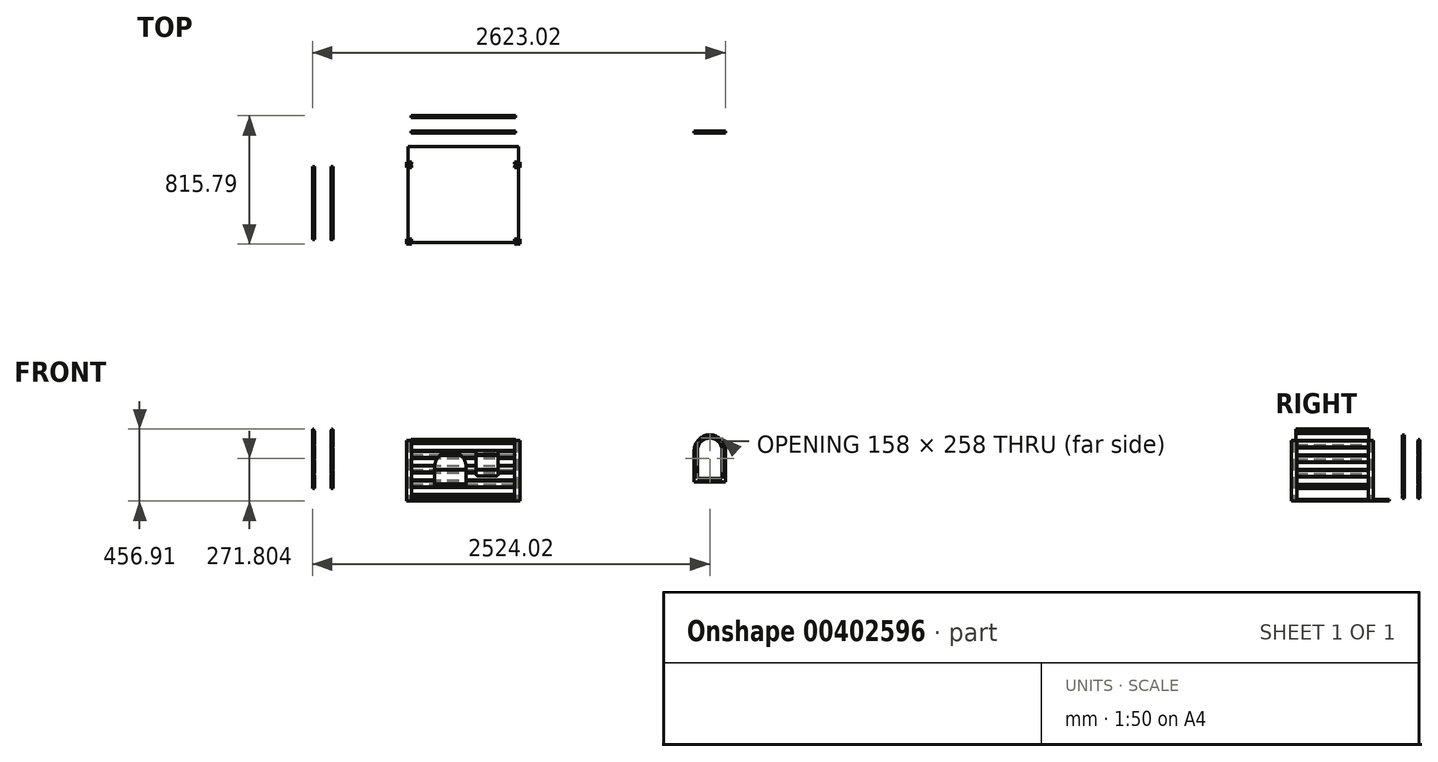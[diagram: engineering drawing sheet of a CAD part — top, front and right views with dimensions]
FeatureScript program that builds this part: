
annotation { "Feature Type Name" : "Feature", "Feature Type Description" : "" }
export const myFeature = defineFeature(function(context is Context, id is Id, definition is map)
    precondition{}
    {
        {
            var Q0;
            Q0=qCreatedBy(makeId("Top.planeOp"),FACE);
            var sketch = newSketch(context, id + "F0", { "sketchPlane" : qUnion([Q0])});
            skLineSegment(sketch, "E0.bottom", {"start": v(-350, -250) * mm, "end": v(350, -250) * mm});
            skLineSegment(sketch, "E0.top", {"start": v(-350, 360) * mm, "end": v(350, 360) * mm});
            skLineSegment(sketch, "E0.left", {"start": v(-350, -250) * mm, "end": v(-350, 360) * mm});
            skLineSegment(sketch, "E0.right", {"start": v(350, -250) * mm, "end": v(350, 360) * mm});
            skPoint(sketch, "E0.middle", {"position": v(0, 0) * mm});
            skSolve(sketch);
        }
        {
            var Q0;
            Q0=makeQuery(id+"F0.imprint","IMPRINT",FACE,{"disambiguationData":[TD([[makeQuery(id+"F0.imprint","IMPRINT",EDGE,{"derivedFrom":sQuery(id+"F0.wireOp",EDGE,"E0.bottom")}),1.0]])]});
            extrude(context, id + "F1", {"entities" : qUnion([Q0]), "depth" : 12 * mm});
        }
        {
            var Q0;
            Q0=makeQuery(id+"F1.opExtrude","CAP_FACE",FACE,{"disambiguationData":[OSD([sQuery(id+"F0.wireOp",EDGE,"E0.bottom"),sQuery(id+"F0.wireOp",EDGE,"E0.top"),sQuery(id+"F0.wireOp",EDGE,"E0.left"),sQuery(id+"F0.wireOp",EDGE,"E0.right")])],"isStart":true});
            var sketch = newSketch(context, id + "F2", { "sketchPlane" : qUnion([Q0])});
            skLineSegment(sketch, "E1.bottom", {"start": v(-326.75, 226.75) * mm, "end": v(-337.5, 226.75) * mm});
            skLineSegment(sketch, "E1.top", {"start": v(-326.75, 260.75) * mm, "end": v(-360.75, 260.75) * mm});
            skLineSegment(sketch, "E1.left", {"start": v(-326.75, 226.75) * mm, "end": v(-326.75, 237.5) * mm});
            skLineSegment(sketch, "E1.right", {"start": v(-360.75, 226.75) * mm, "end": v(-360.75, 260.75) * mm});
            skPoint(sketch, "E1.middle", {"position": v(-343.75, 243.75) * mm});
            skLineSegment(sketch, "E2.bottom", {"start": v(-337.5, 231.75) * mm, "end": v(-350, 231.75) * mm});
            skLineSegment(sketch, "E2.left", {"start": v(-337.5, 231.75) * mm, "end": v(-337.5, 226.75) * mm});
            skLineSegment(sketch, "E2.right", {"start": v(-350, 231.75) * mm, "end": v(-350, 226.75) * mm});
            skPoint(sketch, "E2.middle", {"position": v(-343.75, 226.75) * mm});
            skLineSegment(sketch, "E3.bottom", {"start": v(-331.75, 250) * mm, "end": v(-326.75, 250) * mm});
            skLineSegment(sketch, "E3.top", {"start": v(-331.75, 237.5) * mm, "end": v(-326.75, 237.5) * mm});
            skLineSegment(sketch, "E3.left", {"start": v(-331.75, 250) * mm, "end": v(-331.75, 237.5) * mm});
            skPoint(sketch, "E3.middle", {"position": v(-326.75, 243.75) * mm});
            skLineSegment(sketch, "E4", {"start": v(-350, 250) * mm, "end": v(-350, 231.75) * mm});
            skLineSegment(sketch, "E5.trimOffspring", {"start": v(-350, 226.75) * mm, "end": v(-360.75, 226.75) * mm});
            skLineSegment(sketch, "E6.trimOffspring", {"start": v(-326.75, 250) * mm, "end": v(-326.75, 260.75) * mm});
            skPoint(sketch, "E7", {"position": v(-350, 231.75) * mm});
            skLineSegment(sketch, "E8.MirrorCS", {"start": v(350, 231.75) * mm, "end": v(350, 226.75) * mm});
            skLineSegment(sketch, "E9.MirrorCS", {"start": v(337.5, 231.75) * mm, "end": v(350, 231.75) * mm});
            skLineSegment(sketch, "E10.MirrorCS", {"start": v(331.75, 250) * mm, "end": v(331.75, 237.5) * mm});
            skLineSegment(sketch, "E11.MirrorCS", {"start": v(331.75, 250) * mm, "end": v(326.75, 250) * mm});
            skLineSegment(sketch, "E12.MirrorCS", {"start": v(331.75, 237.5) * mm, "end": v(326.75, 237.5) * mm});
            skLineSegment(sketch, "E13.MirrorCS", {"start": v(337.5, 231.75) * mm, "end": v(337.5, 226.75) * mm});
            skLineSegment(sketch, "E14.MirrorCS", {"start": v(326.75, 226.75) * mm, "end": v(326.75, 237.5) * mm});
            skLineSegment(sketch, "E15.MirrorCS", {"start": v(326.75, 250) * mm, "end": v(326.75, 260.75) * mm});
            skLineSegment(sketch, "E16.MirrorCS", {"start": v(326.75, 226.75) * mm, "end": v(337.5, 226.75) * mm});
            skLineSegment(sketch, "E17.MirrorCS", {"start": v(350, 226.75) * mm, "end": v(360.75, 226.75) * mm});
            skLineSegment(sketch, "E18.MirrorCS", {"start": v(350, 250) * mm, "end": v(350, 231.75) * mm});
            skPoint(sketch, "E19.MirrorP", {"position": v(350, 231.75) * mm});
            skLineSegment(sketch, "E20.MirrorCS", {"start": v(326.75, 260.75) * mm, "end": v(360.75, 260.75) * mm});
            skLineSegment(sketch, "E21.MirrorCS", {"start": v(360.75, 226.75) * mm, "end": v(360.75, 260.75) * mm});
            skPoint(sketch, "E22.MirrorP", {"position": v(343.75, 243.75) * mm});
            skPoint(sketch, "E23.MirrorP", {"position": v(343.75, 226.75) * mm});
            skPoint(sketch, "E24.MirrorP", {"position": v(326.75, 243.75) * mm});
            skLineSegment(sketch, "E25.MirrorCS", {"start": v(331.75, -250) * mm, "end": v(331.75, -237.5) * mm});
            skLineSegment(sketch, "E26.MirrorCS", {"start": v(331.75, -250) * mm, "end": v(326.75, -250) * mm});
            skLineSegment(sketch, "E27.MirrorCS", {"start": v(326.75, -250) * mm, "end": v(326.75, -260.75) * mm});
            skLineSegment(sketch, "E28.MirrorCS", {"start": v(350, -250) * mm, "end": v(350, -231.75) * mm});
            skLineSegment(sketch, "E29.MirrorCS", {"start": v(326.75, -260.75) * mm, "end": v(360.75, -260.75) * mm});
            skLineSegment(sketch, "E30.MirrorCS", {"start": v(360.75, -226.75) * mm, "end": v(360.75, -260.75) * mm});
            skLineSegment(sketch, "E31.MirrorCS", {"start": v(350, -231.75) * mm, "end": v(350, -226.75) * mm});
            skLineSegment(sketch, "E32.MirrorCS", {"start": v(-350, -231.75) * mm, "end": v(-350, -226.75) * mm});
            skLineSegment(sketch, "E33.MirrorCS", {"start": v(337.5, -231.75) * mm, "end": v(350, -231.75) * mm});
            skLineSegment(sketch, "E34.MirrorCS", {"start": v(331.75, -237.5) * mm, "end": v(326.75, -237.5) * mm});
            skLineSegment(sketch, "E35.MirrorCS", {"start": v(-337.5, -231.75) * mm, "end": v(-350, -231.75) * mm});
            skLineSegment(sketch, "E36.MirrorCS", {"start": v(-331.75, -250) * mm, "end": v(-331.75, -237.5) * mm});
            skLineSegment(sketch, "E37.MirrorCS", {"start": v(337.5, -231.75) * mm, "end": v(337.5, -226.75) * mm});
            skLineSegment(sketch, "E38.MirrorCS", {"start": v(-331.75, -237.5) * mm, "end": v(-326.75, -237.5) * mm});
            skLineSegment(sketch, "E39.MirrorCS", {"start": v(-337.5, -231.75) * mm, "end": v(-337.5, -226.75) * mm});
            skLineSegment(sketch, "E40.MirrorCS", {"start": v(-331.75, -250) * mm, "end": v(-326.75, -250) * mm});
            skLineSegment(sketch, "E41.MirrorCS", {"start": v(326.75, -226.75) * mm, "end": v(337.5, -226.75) * mm});
            skLineSegment(sketch, "E42.MirrorCS", {"start": v(326.75, -226.75) * mm, "end": v(326.75, -237.5) * mm});
            skLineSegment(sketch, "E43.MirrorCS", {"start": v(-326.75, -226.75) * mm, "end": v(-337.5, -226.75) * mm});
            skLineSegment(sketch, "E44.MirrorCS", {"start": v(-326.75, -226.75) * mm, "end": v(-326.75, -237.5) * mm});
            skLineSegment(sketch, "E45.MirrorCS", {"start": v(-326.75, -250) * mm, "end": v(-326.75, -260.75) * mm});
            skLineSegment(sketch, "E46.MirrorCS", {"start": v(350, -226.75) * mm, "end": v(360.75, -226.75) * mm});
            skLineSegment(sketch, "E47.MirrorCS", {"start": v(-350, -226.75) * mm, "end": v(-360.75, -226.75) * mm});
            skLineSegment(sketch, "E48.MirrorCS", {"start": v(-350, -250) * mm, "end": v(-350, -231.75) * mm});
            skPoint(sketch, "E49.MirrorP", {"position": v(343.75, -226.75) * mm});
            skPoint(sketch, "E50.MirrorP", {"position": v(-326.75, -243.75) * mm});
            skLineSegment(sketch, "E51.MirrorCS", {"start": v(-360.75, -226.75) * mm, "end": v(-360.75, -260.75) * mm});
            skLineSegment(sketch, "E52.MirrorCS", {"start": v(-326.75, -260.75) * mm, "end": v(-360.75, -260.75) * mm});
            skPoint(sketch, "E53.MirrorP", {"position": v(350, -231.75) * mm});
            skPoint(sketch, "E54.MirrorP", {"position": v(-343.75, -226.75) * mm});
            skPoint(sketch, "E55.MirrorP", {"position": v(-343.75, -243.75) * mm});
            skPoint(sketch, "E56.MirrorP", {"position": v(326.75, -243.75) * mm});
            skPoint(sketch, "E57.MirrorP", {"position": v(-350, -231.75) * mm});
            skPoint(sketch, "E58.MirrorP", {"position": v(343.75, -243.75) * mm});
            skLineSegment(sketch, "E59", {"start": v(-350, -250) * mm, "end": v(-350, -260.75) * mm});
            skLineSegment(sketch, "E60", {"start": v(350, -250) * mm, "end": v(350, -260.75) * mm});
            skSolve(sketch);
        }
        {
            var Q0;
            Q0=makeQuery(id+"F2.imprint","IMPRINT",FACE,{"disambiguationData":[TD([[makeQuery(id+"F2.imprint","IMPRINT",EDGE,{"derivedFrom":sQuery(id+"F2.wireOp",EDGE,"E1.top")}),1.0]])]});
            var Q1;
            Q1=makeQuery(id+"F2.imprint","IMPRINT",FACE,{"disambiguationData":[TD([[makeQuery(id+"F2.imprint","IMPRINT",EDGE,{"derivedFrom":sQuery(id+"F2.wireOp",EDGE,"E32.MirrorCS")}),-1.0]])]});
            var Q2;
            Q2=makeQuery(id+"F2.imprint","IMPRINT",FACE,{"disambiguationData":[TD([[makeQuery(id+"F2.imprint","IMPRINT",EDGE,{"derivedFrom":sQuery(id+"F2.wireOp",EDGE,"E8.MirrorCS")}),1.0]])]});
            var Q3;
            Q3=makeQuery(id+"F2.imprint","IMPRINT",FACE,{"disambiguationData":[TD([[makeQuery(id+"F2.imprint","IMPRINT",EDGE,{"derivedFrom":sQuery(id+"F2.wireOp",EDGE,"E28.MirrorCS")}),1.0]])]});
            extrude(context, id + "F3", {"entities" : qUnion([Q0, Q1, Q2, Q3]), "oppositeDirection" : true, "depth" : 384 * mm});
        }
        {
            var Q0;
            Q0=makeQuery(id+"F2.imprint","IMPRINT",FACE,{"disambiguationData":[TD([[makeQuery(id+"F2.imprint","IMPRINT",EDGE,{"derivedFrom":sQuery(id+"F2.wireOp",EDGE,"E9.MirrorCS")}),1.0]])]});
            var Q1;
            Q1=makeQuery(id+"F2.imprint","IMPRINT",FACE,{"disambiguationData":[TD([[makeQuery(id+"F2.imprint","IMPRINT",EDGE,{"derivedFrom":sQuery(id+"F2.wireOp",EDGE,"E1.bottom")}),-1.0]])]});
            var Q2;
            {var subQ1=sQuery(id+"F2.wireOp",EDGE,"E25.MirrorCS");Q2=makeQuery(id+"F2.imprint","IMPRINT",FACE,{"disambiguationData":[TD([[makeQuery(id+"F2.imprint","IMPRINT",EDGE,{"derivedFrom":subQ1}),-1.0]])]});}
            var Q3;
            Q3=makeQuery(id+"F2.imprint","IMPRINT",FACE,{"disambiguationData":[TD([[makeQuery(id+"F2.imprint","IMPRINT",EDGE,{"derivedFrom":sQuery(id+"F2.wireOp",EDGE,"E35.MirrorCS")}),1.0]])]});
            var Q4;
            {var subQ3=sQuery(id+"F2.wireOp",EDGE,"E40.MirrorCS");Q4=makeQuery(id+"F2.imprint","IMPRINT",FACE,{"disambiguationData":[TD([[makeQuery(id+"F2.imprint","IMPRINT",EDGE,{"derivedFrom":subQ3}),-1.0]])]});}
            extrude(context, id + "F4", {"entities" : qUnion([Q0, Q1, Q2, Q3, Q4]), "oppositeDirection" : true, "depth" : 384 * mm, "hasSecondDirection" : true, "secondDirectionOppositeDirection" : true, "secondDirectionDepth" : 12 * mm});
        }
        {
            var Q0;
            Q0=makeQuery(id+"F4.opExtrude","SWEPT_FACE",FACE,{"disambiguationData":[OSD([sQuery(id+"F2.wireOp",EDGE,"E33.MirrorCS")])]});
            var sketch = newSketch(context, id + "F5", { "sketchPlane" : qUnion([Q0])});
            skLineSegment(sketch, "E61", {"start": v(-893, 200.64) * mm, "end": v(-893, 47.68) * mm});
            skLineSegment(sketch, "E62.MirrorCS", {"start": v(-951.9, 177.9) * mm, "end": v(-953.9, 177.9) * mm});
            skLineSegment(sketch, "E63.MirrorCS", {"start": v(-951.9, 177.9) * mm, "end": v(-949.9, 177.9) * mm});
            skLineSegment(sketch, "E64.MirrorCS", {"start": v(-949.9, 177.9) * mm, "end": v(-953.9, 177.9) * mm});
            skLineSegment(sketch, "E65.MirrorCS", {"start": v(-949.9, 170.9) * mm, "end": v(-949.64, 170.9) * mm});
            skLineSegment(sketch, "E66.MirrorCS", {"start": v(-953.9, 177.9) * mm, "end": v(-953.9, 174.9) * mm});
            skLineSegment(sketch, "E67.MirrorCS", {"start": v(-949.9, 81.9) * mm, "end": v(-949.9, 84.9) * mm});
            skLineSegment(sketch, "E68.MirrorCS", {"start": v(-953.9, 81.9) * mm, "end": v(-953.9, 84.9) * mm});
            skLineSegment(sketch, "E69.MirrorCS", {"start": v(-953.9, 84.9) * mm, "end": v(-949.9, 84.9) * mm});
            skLineSegment(sketch, "E70.MirrorCS", {"start": v(-945.64, 81.9) * mm, "end": v(-949.9, 81.9) * mm});
            skLineSegment(sketch, "E71.MirrorCS", {"start": v(-953.9, 81.9) * mm, "end": v(-958.14, 81.9) * mm});
            skArc(sketch, "E72.MirrorCS", {"start": v(-958.14, 152.4) * mm, "mid": v(-955.64, 154.9) * mm, "end": v(-958.14, 157.4) * mm});
            skArc(sketch, "E73.MirrorCS", {"start": v(-945.64, 166.9) * mm, "mid": v(-946.82, 169.73) * mm, "end": v(-949.64, 170.9) * mm});
            skArc(sketch, "E74.MirrorCS", {"start": v(-958.14, 102.4) * mm, "mid": v(-955.64, 104.9) * mm, "end": v(-958.14, 107.4) * mm});
            skLineSegment(sketch, "E75.MirrorCS", {"start": v(-958.14, 129.9) * mm, "end": v(-958.14, 107.4) * mm});
            skLineSegment(sketch, "E76.MirrorCS", {"start": v(-945.64, 81.9) * mm, "end": v(-945.64, 166.9) * mm});
            skLineSegment(sketch, "E77.MirrorCS", {"start": v(-949.9, 177.9) * mm, "end": v(-949.9, 170.9) * mm});
            skPoint(sketch, "E78.MirrorP", {"position": v(-953.9, 80.4) * mm});
            skPoint(sketch, "E79.MirrorP", {"position": v(-945.64, 170.9) * mm});
            skPoint(sketch, "E80.MirrorP", {"position": v(-949.9, 80.4) * mm});
            skLineSegment(sketch, "E81.MirrorCS", {"start": v(-958.14, 81.9) * mm, "end": v(-958.14, 102.4) * mm});
            skLineSegment(sketch, "E82.MirrorCS", {"start": v(-958.14, 107.4) * mm, "end": v(-958.14, 154.9) * mm});
            skPoint(sketch, "E83.MirrorP", {"position": v(-951.9, 81.9) * mm});
            skLineSegment(sketch, "E84.MirrorCS", {"start": v(-958.14, 129.9) * mm, "end": v(-958.14, 152.4) * mm});
            skLineSegment(sketch, "E85.MirrorCS", {"start": v(-958.14, 157.4) * mm, "end": v(-958.14, 174.9) * mm});
            skPoint(sketch, "E86.MirrorP", {"position": v(-951.9, 129.9) * mm});
            skPoint(sketch, "E87.MirrorP", {"position": v(-958.14, 177.9) * mm});
            skLineSegment(sketch, "E88.MirrorCS", {"start": v(-951.9, 270.9) * mm, "end": v(-953.9, 270.9) * mm});
            skLineSegment(sketch, "E89.MirrorCS", {"start": v(-951.9, 270.9) * mm, "end": v(-949.9, 270.9) * mm});
            skLineSegment(sketch, "E90.MirrorCS", {"start": v(-949.9, 270.9) * mm, "end": v(-953.9, 270.9) * mm});
            skLineSegment(sketch, "E91.MirrorCS", {"start": v(-949.9, 263.9) * mm, "end": v(-949.64, 263.9) * mm});
            skLineSegment(sketch, "E92.MirrorCS", {"start": v(-953.9, 270.9) * mm, "end": v(-953.9, 267.9) * mm});
            skLineSegment(sketch, "E93.MirrorCS", {"start": v(-949.9, 174.9) * mm, "end": v(-949.9, 177.9) * mm});
            skLineSegment(sketch, "E94.MirrorCS", {"start": v(-953.9, 174.9) * mm, "end": v(-953.9, 177.9) * mm});
            skLineSegment(sketch, "E95.MirrorCS", {"start": v(-953.9, 177.9) * mm, "end": v(-949.9, 177.9) * mm});
            skLineSegment(sketch, "E96.MirrorCS", {"start": v(-945.64, 174.9) * mm, "end": v(-949.9, 174.9) * mm});
            skArc(sketch, "E97.MirrorCS", {"start": v(-958.14, 245.4) * mm, "mid": v(-955.64, 247.9) * mm, "end": v(-958.14, 250.4) * mm});
            skArc(sketch, "E98.MirrorCS", {"start": v(-945.64, 259.9) * mm, "mid": v(-946.82, 262.73) * mm, "end": v(-949.64, 263.9) * mm});
            skArc(sketch, "E99.MirrorCS", {"start": v(-958.14, 195.4) * mm, "mid": v(-955.64, 197.9) * mm, "end": v(-958.14, 200.4) * mm});
            skLineSegment(sketch, "E100.MirrorCS", {"start": v(-958.14, 222.9) * mm, "end": v(-958.14, 200.4) * mm});
            skLineSegment(sketch, "E101.MirrorCS", {"start": v(-945.64, 174.9) * mm, "end": v(-945.64, 259.9) * mm});
            skLineSegment(sketch, "E102.MirrorCS", {"start": v(-949.9, 270.9) * mm, "end": v(-949.9, 263.9) * mm});
            skPoint(sketch, "E103.MirrorP", {"position": v(-953.9, 173.4) * mm});
            skPoint(sketch, "E104.MirrorP", {"position": v(-945.64, 263.9) * mm});
            skPoint(sketch, "E105.MirrorP", {"position": v(-949.9, 173.4) * mm});
            skLineSegment(sketch, "E106.MirrorCS", {"start": v(-958.14, 174.9) * mm, "end": v(-958.14, 195.4) * mm});
            skLineSegment(sketch, "E107.MirrorCS", {"start": v(-958.14, 200.4) * mm, "end": v(-958.14, 247.9) * mm});
            skPoint(sketch, "E108.MirrorP", {"position": v(-951.9, 174.9) * mm});
            skLineSegment(sketch, "E109.MirrorCS", {"start": v(-958.14, 222.9) * mm, "end": v(-958.14, 245.4) * mm});
            skLineSegment(sketch, "E110.MirrorCS", {"start": v(-958.14, 250.4) * mm, "end": v(-958.14, 267.9) * mm});
            skPoint(sketch, "E111.MirrorP", {"position": v(-951.9, 222.9) * mm});
            skPoint(sketch, "E112.MirrorP", {"position": v(-958.14, 270.9) * mm});
            skLineSegment(sketch, "E113.MirrorCS", {"start": v(-951.9, 363.9) * mm, "end": v(-953.9, 363.9) * mm});
            skLineSegment(sketch, "E114.MirrorCS", {"start": v(-951.9, 363.9) * mm, "end": v(-949.9, 363.9) * mm});
            skLineSegment(sketch, "E115.MirrorCS", {"start": v(-949.9, 363.9) * mm, "end": v(-953.9, 363.9) * mm});
            skLineSegment(sketch, "E116.MirrorCS", {"start": v(-949.9, 356.9) * mm, "end": v(-949.64, 356.9) * mm});
            skLineSegment(sketch, "E117.MirrorCS", {"start": v(-953.9, 363.9) * mm, "end": v(-953.9, 360.9) * mm});
            skLineSegment(sketch, "E118.MirrorCS", {"start": v(-949.9, 267.9) * mm, "end": v(-949.9, 270.9) * mm});
            skLineSegment(sketch, "E119.MirrorCS", {"start": v(-953.9, 267.9) * mm, "end": v(-953.9, 270.9) * mm});
            skLineSegment(sketch, "E120.MirrorCS", {"start": v(-953.9, 270.9) * mm, "end": v(-949.9, 270.9) * mm});
            skLineSegment(sketch, "E121.MirrorCS", {"start": v(-945.64, 267.9) * mm, "end": v(-949.9, 267.9) * mm});
            skArc(sketch, "E122.MirrorCS", {"start": v(-958.14, 338.4) * mm, "mid": v(-955.64, 340.9) * mm, "end": v(-958.14, 343.4) * mm});
            skArc(sketch, "E123.MirrorCS", {"start": v(-945.64, 352.9) * mm, "mid": v(-946.82, 355.73) * mm, "end": v(-949.64, 356.9) * mm});
            skArc(sketch, "E124.MirrorCS", {"start": v(-958.14, 288.4) * mm, "mid": v(-955.64, 290.9) * mm, "end": v(-958.14, 293.4) * mm});
            skLineSegment(sketch, "E125.MirrorCS", {"start": v(-958.14, 315.9) * mm, "end": v(-958.14, 293.4) * mm});
            skLineSegment(sketch, "E126.MirrorCS", {"start": v(-945.64, 267.9) * mm, "end": v(-945.64, 352.9) * mm});
            skLineSegment(sketch, "E127.MirrorCS", {"start": v(-949.9, 363.9) * mm, "end": v(-949.9, 356.9) * mm});
            skPoint(sketch, "E128.MirrorP", {"position": v(-953.9, 266.4) * mm});
            skPoint(sketch, "E129.MirrorP", {"position": v(-945.64, 356.9) * mm});
            skPoint(sketch, "E130.MirrorP", {"position": v(-949.9, 266.4) * mm});
            skLineSegment(sketch, "E131.MirrorCS", {"start": v(-958.14, 267.9) * mm, "end": v(-958.14, 288.4) * mm});
            skLineSegment(sketch, "E132.MirrorCS", {"start": v(-958.14, 293.4) * mm, "end": v(-958.14, 340.9) * mm});
            skPoint(sketch, "E133.MirrorP", {"position": v(-951.9, 267.9) * mm});
            skLineSegment(sketch, "E134.MirrorCS", {"start": v(-958.14, 315.9) * mm, "end": v(-958.14, 338.4) * mm});
            skLineSegment(sketch, "E135.MirrorCS", {"start": v(-958.14, 343.4) * mm, "end": v(-958.14, 360.9) * mm});
            skPoint(sketch, "E136.MirrorP", {"position": v(-951.9, 315.9) * mm});
            skPoint(sketch, "E137.MirrorP", {"position": v(-958.14, 363.9) * mm});
            skLineSegment(sketch, "E138.MirrorCS", {"start": v(-951.9, 456.9) * mm, "end": v(-953.9, 456.9) * mm});
            skLineSegment(sketch, "E139.MirrorCS", {"start": v(-951.9, 456.9) * mm, "end": v(-949.9, 456.9) * mm});
            skLineSegment(sketch, "E140.MirrorCS", {"start": v(-949.9, 456.9) * mm, "end": v(-953.9, 456.9) * mm});
            skLineSegment(sketch, "E141.MirrorCS", {"start": v(-949.9, 449.9) * mm, "end": v(-949.64, 449.9) * mm});
            skLineSegment(sketch, "E142.MirrorCS", {"start": v(-953.9, 456.9) * mm, "end": v(-953.9, 453.9) * mm});
            skLineSegment(sketch, "E143.MirrorCS", {"start": v(-949.9, 360.9) * mm, "end": v(-949.9, 363.9) * mm});
            skLineSegment(sketch, "E144.MirrorCS", {"start": v(-953.9, 360.9) * mm, "end": v(-953.9, 363.9) * mm});
            skLineSegment(sketch, "E145.MirrorCS", {"start": v(-953.9, 363.9) * mm, "end": v(-949.9, 363.9) * mm});
            skLineSegment(sketch, "E146.MirrorCS", {"start": v(-945.64, 360.9) * mm, "end": v(-949.9, 360.9) * mm});
            skArc(sketch, "E147.MirrorCS", {"start": v(-958.14, 431.4) * mm, "mid": v(-955.64, 433.9) * mm, "end": v(-958.14, 436.4) * mm});
            skArc(sketch, "E148.MirrorCS", {"start": v(-945.64, 445.9) * mm, "mid": v(-946.82, 448.73) * mm, "end": v(-949.64, 449.9) * mm});
            skArc(sketch, "E149.MirrorCS", {"start": v(-958.14, 381.4) * mm, "mid": v(-955.64, 383.9) * mm, "end": v(-958.14, 386.4) * mm});
            skLineSegment(sketch, "E150.MirrorCS", {"start": v(-958.14, 408.9) * mm, "end": v(-958.14, 386.4) * mm});
            skLineSegment(sketch, "E151.MirrorCS", {"start": v(-945.64, 360.9) * mm, "end": v(-945.64, 445.9) * mm});
            skLineSegment(sketch, "E152.MirrorCS", {"start": v(-949.9, 456.9) * mm, "end": v(-949.9, 449.9) * mm});
            skPoint(sketch, "E153.MirrorP", {"position": v(-953.9, 359.4) * mm});
            skPoint(sketch, "E154.MirrorP", {"position": v(-945.64, 449.9) * mm});
            skPoint(sketch, "E155.MirrorP", {"position": v(-949.9, 359.4) * mm});
            skLineSegment(sketch, "E156.MirrorCS", {"start": v(-958.14, 360.9) * mm, "end": v(-958.14, 381.4) * mm});
            skLineSegment(sketch, "E157.MirrorCS", {"start": v(-958.14, 386.4) * mm, "end": v(-958.14, 433.9) * mm});
            skPoint(sketch, "E158.MirrorP", {"position": v(-951.9, 360.9) * mm});
            skLineSegment(sketch, "E159.MirrorCS", {"start": v(-958.14, 408.9) * mm, "end": v(-958.14, 431.4) * mm});
            skLineSegment(sketch, "E160.MirrorCS", {"start": v(-958.14, 436.4) * mm, "end": v(-958.14, 453.9) * mm});
            skPoint(sketch, "E161.MirrorP", {"position": v(-951.9, 408.9) * mm});
            skPoint(sketch, "E162.MirrorP", {"position": v(-958.14, 456.9) * mm});
            skLineSegment(sketch, "E163", {"start": v(-953.9, 453.9) * mm, "end": v(-958.14, 453.9) * mm});
            skLineSegment(sketch, "E164.MirrorCS", {"start": v(-836.12, 270.9) * mm, "end": v(-832.12, 270.9) * mm});
            skLineSegment(sketch, "E165.MirrorCS", {"start": v(-834.12, 363.9) * mm, "end": v(-832.12, 363.9) * mm});
            skLineSegment(sketch, "E166.MirrorCS", {"start": v(-832.12, 270.9) * mm, "end": v(-832.12, 267.9) * mm});
            skLineSegment(sketch, "E167.MirrorCS", {"start": v(-832.12, 363.9) * mm, "end": v(-836.12, 363.9) * mm});
            skLineSegment(sketch, "E168.MirrorCS", {"start": v(-836.12, 263.9) * mm, "end": v(-836.37, 263.9) * mm});
            skLineSegment(sketch, "E169.MirrorCS", {"start": v(-834.12, 270.9) * mm, "end": v(-836.12, 270.9) * mm});
            skLineSegment(sketch, "E170.MirrorCS", {"start": v(-834.12, 363.9) * mm, "end": v(-836.12, 363.9) * mm});
            skLineSegment(sketch, "E171.MirrorCS", {"start": v(-832.12, 270.9) * mm, "end": v(-836.12, 270.9) * mm});
            skLineSegment(sketch, "E172.MirrorCS", {"start": v(-836.12, 363.9) * mm, "end": v(-832.12, 363.9) * mm});
            skLineSegment(sketch, "E173.MirrorCS", {"start": v(-834.12, 270.9) * mm, "end": v(-832.12, 270.9) * mm});
            skLineSegment(sketch, "E174.MirrorCS", {"start": v(-836.12, 267.9) * mm, "end": v(-836.12, 270.9) * mm});
            skLineSegment(sketch, "E175.MirrorCS", {"start": v(-836.12, 360.9) * mm, "end": v(-836.12, 363.9) * mm});
            skLineSegment(sketch, "E176.MirrorCS", {"start": v(-832.12, 267.9) * mm, "end": v(-832.12, 270.9) * mm});
            skLineSegment(sketch, "E177.MirrorCS", {"start": v(-832.12, 363.9) * mm, "end": v(-832.12, 360.9) * mm});
            skLineSegment(sketch, "E178.MirrorCS", {"start": v(-836.12, 270.9) * mm, "end": v(-836.12, 263.9) * mm});
            skLineSegment(sketch, "E179.MirrorCS", {"start": v(-836.12, 363.9) * mm, "end": v(-836.12, 356.9) * mm});
            skLineSegment(sketch, "E180.MirrorCS", {"start": v(-832.12, 177.9) * mm, "end": v(-836.12, 177.9) * mm});
            skLineSegment(sketch, "E181.MirrorCS", {"start": v(-840.37, 267.9) * mm, "end": v(-836.12, 267.9) * mm});
            skLineSegment(sketch, "E182.MirrorCS", {"start": v(-836.12, 356.9) * mm, "end": v(-836.37, 356.9) * mm});
            skArc(sketch, "E183.MirrorCS", {"start": v(-840.37, 259.9) * mm, "mid": v(-839.2, 262.73) * mm, "end": v(-836.37, 263.9) * mm});
            skLineSegment(sketch, "E184.MirrorCS", {"start": v(-836.12, 174.9) * mm, "end": v(-836.12, 177.9) * mm});
            skArc(sketch, "E185.MirrorCS", {"start": v(-840.37, 352.9) * mm, "mid": v(-839.2, 355.73) * mm, "end": v(-836.37, 356.9) * mm});
            skLineSegment(sketch, "E186.MirrorCS", {"start": v(-840.37, 360.9) * mm, "end": v(-836.12, 360.9) * mm});
            skLineSegment(sketch, "E187.MirrorCS", {"start": v(-832.12, 360.9) * mm, "end": v(-832.12, 363.9) * mm});
            skLineSegment(sketch, "E188.MirrorCS", {"start": v(-834.12, 177.9) * mm, "end": v(-832.12, 177.9) * mm});
            skLineSegment(sketch, "E189.MirrorCS", {"start": v(-836.12, 177.9) * mm, "end": v(-836.12, 170.9) * mm});
            skLineSegment(sketch, "E190.MirrorCS", {"start": v(-832.12, 174.9) * mm, "end": v(-832.12, 177.9) * mm});
            skLineSegment(sketch, "E191.MirrorCS", {"start": v(-836.12, 177.9) * mm, "end": v(-832.12, 177.9) * mm});
            skLineSegment(sketch, "E192.MirrorCS", {"start": v(-834.12, 177.9) * mm, "end": v(-836.12, 177.9) * mm});
            skLineSegment(sketch, "E193.MirrorCS", {"start": v(-836.12, 170.9) * mm, "end": v(-836.37, 170.9) * mm});
            skLineSegment(sketch, "E194.MirrorCS", {"start": v(-840.37, 174.9) * mm, "end": v(-836.12, 174.9) * mm});
            skArc(sketch, "E195.MirrorCS", {"start": v(-840.37, 166.9) * mm, "mid": v(-839.2, 169.73) * mm, "end": v(-836.37, 170.9) * mm});
            skLineSegment(sketch, "E196.MirrorCS", {"start": v(-832.12, 177.9) * mm, "end": v(-832.12, 174.9) * mm});
            skLineSegment(sketch, "E197.MirrorCS", {"start": v(-834.12, 456.9) * mm, "end": v(-832.12, 456.9) * mm});
            skLineSegment(sketch, "E198.MirrorCS", {"start": v(-832.12, 84.9) * mm, "end": v(-836.12, 84.9) * mm});
            skLineSegment(sketch, "E199.MirrorCS", {"start": v(-834.12, 456.9) * mm, "end": v(-836.12, 456.9) * mm});
            skLineSegment(sketch, "E200.MirrorCS", {"start": v(-832.12, 456.9) * mm, "end": v(-832.12, 453.9) * mm});
            skLineSegment(sketch, "E201.MirrorCS", {"start": v(-827.87, 157.4) * mm, "end": v(-827.87, 174.9) * mm});
            skLineSegment(sketch, "E202.MirrorCS", {"start": v(-836.12, 81.9) * mm, "end": v(-836.12, 84.9) * mm});
            skLineSegment(sketch, "E203.MirrorCS", {"start": v(-836.12, 456.9) * mm, "end": v(-832.12, 456.9) * mm});
            skArc(sketch, "E204.MirrorCS", {"start": v(-840.37, 445.9) * mm, "mid": v(-839.2, 448.73) * mm, "end": v(-836.37, 449.9) * mm});
            skLineSegment(sketch, "E205.MirrorCS", {"start": v(-827.87, 250.4) * mm, "end": v(-827.87, 267.9) * mm});
            skLineSegment(sketch, "E206.MirrorCS", {"start": v(-827.87, 436.4) * mm, "end": v(-827.87, 453.9) * mm});
            skLineSegment(sketch, "E207.MirrorCS", {"start": v(-836.12, 456.9) * mm, "end": v(-836.12, 449.9) * mm});
            skLineSegment(sketch, "E208.MirrorCS", {"start": v(-836.12, 449.9) * mm, "end": v(-836.37, 449.9) * mm});
            skLineSegment(sketch, "E209.MirrorCS", {"start": v(-832.12, 81.9) * mm, "end": v(-832.12, 84.9) * mm});
            skArc(sketch, "E210.MirrorCS", {"start": v(-827.87, 152.4) * mm, "mid": v(-830.37, 154.9) * mm, "end": v(-827.87, 157.4) * mm});
            skLineSegment(sketch, "E211.MirrorCS", {"start": v(-832.12, 453.9) * mm, "end": v(-827.87, 453.9) * mm});
            skLineSegment(sketch, "E212.MirrorCS", {"start": v(-827.87, 174.9) * mm, "end": v(-827.87, 195.4) * mm});
            skLineSegment(sketch, "E213.MirrorCS", {"start": v(-827.87, 360.9) * mm, "end": v(-827.87, 381.4) * mm});
            skArc(sketch, "E214.MirrorCS", {"start": v(-827.87, 381.4) * mm, "mid": v(-830.37, 383.9) * mm, "end": v(-827.87, 386.4) * mm});
            skLineSegment(sketch, "E215.MirrorCS", {"start": v(-827.87, 81.9) * mm, "end": v(-827.87, 102.4) * mm});
            skLineSegment(sketch, "E216.MirrorCS", {"start": v(-827.87, 343.4) * mm, "end": v(-827.87, 360.9) * mm});
            skLineSegment(sketch, "E217.MirrorCS", {"start": v(-840.37, 81.9) * mm, "end": v(-836.12, 81.9) * mm});
            skArc(sketch, "E218.MirrorCS", {"start": v(-827.87, 245.4) * mm, "mid": v(-830.37, 247.9) * mm, "end": v(-827.87, 250.4) * mm});
            skArc(sketch, "E219.MirrorCS", {"start": v(-827.87, 338.4) * mm, "mid": v(-830.37, 340.9) * mm, "end": v(-827.87, 343.4) * mm});
            skLineSegment(sketch, "E220.MirrorCS", {"start": v(-832.12, 81.9) * mm, "end": v(-827.87, 81.9) * mm});
            skArc(sketch, "E221.MirrorCS", {"start": v(-827.87, 195.4) * mm, "mid": v(-830.37, 197.9) * mm, "end": v(-827.87, 200.4) * mm});
            skLineSegment(sketch, "E222.MirrorCS", {"start": v(-827.87, 267.9) * mm, "end": v(-827.87, 288.4) * mm});
            skArc(sketch, "E223.MirrorCS", {"start": v(-827.87, 288.4) * mm, "mid": v(-830.37, 290.9) * mm, "end": v(-827.87, 293.4) * mm});
            skArc(sketch, "E224.MirrorCS", {"start": v(-827.87, 102.4) * mm, "mid": v(-830.37, 104.9) * mm, "end": v(-827.87, 107.4) * mm});
            skArc(sketch, "E225.MirrorCS", {"start": v(-827.87, 431.4) * mm, "mid": v(-830.37, 433.9) * mm, "end": v(-827.87, 436.4) * mm});
            skLineSegment(sketch, "E226.MirrorCS", {"start": v(-827.87, 107.4) * mm, "end": v(-827.87, 154.9) * mm});
            skLineSegment(sketch, "E227.MirrorCS", {"start": v(-827.87, 315.9) * mm, "end": v(-827.87, 338.4) * mm});
            skLineSegment(sketch, "E228.MirrorCS", {"start": v(-827.87, 408.9) * mm, "end": v(-827.87, 386.4) * mm});
            skLineSegment(sketch, "E229.MirrorCS", {"start": v(-827.87, 293.4) * mm, "end": v(-827.87, 340.9) * mm});
            skLineSegment(sketch, "E230.MirrorCS", {"start": v(-827.87, 200.4) * mm, "end": v(-827.87, 247.9) * mm});
            skLineSegment(sketch, "E231.MirrorCS", {"start": v(-827.87, 222.9) * mm, "end": v(-827.87, 245.4) * mm});
            skLineSegment(sketch, "E232.MirrorCS", {"start": v(-827.87, 386.4) * mm, "end": v(-827.87, 433.9) * mm});
            skLineSegment(sketch, "E233.MirrorCS", {"start": v(-827.87, 315.9) * mm, "end": v(-827.87, 293.4) * mm});
            skLineSegment(sketch, "E234.MirrorCS", {"start": v(-827.87, 408.9) * mm, "end": v(-827.87, 431.4) * mm});
            skLineSegment(sketch, "E235.MirrorCS", {"start": v(-827.87, 129.9) * mm, "end": v(-827.87, 152.4) * mm});
            skLineSegment(sketch, "E236.MirrorCS", {"start": v(-827.87, 222.9) * mm, "end": v(-827.87, 200.4) * mm});
            skLineSegment(sketch, "E237.MirrorCS", {"start": v(-827.87, 129.9) * mm, "end": v(-827.87, 107.4) * mm});
            skPoint(sketch, "E238.MirrorP", {"position": v(-832.12, 266.4) * mm});
            skPoint(sketch, "E239.MirrorP", {"position": v(-832.12, 173.4) * mm});
            skLineSegment(sketch, "E240.MirrorCS", {"start": v(-840.37, 174.9) * mm, "end": v(-840.37, 259.9) * mm});
            skPoint(sketch, "E241.MirrorP", {"position": v(-834.12, 174.9) * mm});
            skPoint(sketch, "E242.MirrorP", {"position": v(-834.12, 267.9) * mm});
            skPoint(sketch, "E243.MirrorP", {"position": v(-836.12, 266.4) * mm});
            skPoint(sketch, "E244.MirrorP", {"position": v(-840.37, 263.9) * mm});
            skPoint(sketch, "E245.MirrorP", {"position": v(-836.12, 173.4) * mm});
            skLineSegment(sketch, "E246.MirrorCS", {"start": v(-840.37, 267.9) * mm, "end": v(-840.37, 352.9) * mm});
            skPoint(sketch, "E247.MirrorP", {"position": v(-827.87, 177.9) * mm});
            skPoint(sketch, "E248.MirrorP", {"position": v(-840.37, 356.9) * mm});
            skPoint(sketch, "E249.MirrorP", {"position": v(-834.12, 222.9) * mm});
            skPoint(sketch, "E250.MirrorP", {"position": v(-836.12, 80.4) * mm});
            skPoint(sketch, "E251.MirrorP", {"position": v(-840.37, 449.9) * mm});
            skPoint(sketch, "E252.MirrorP", {"position": v(-834.12, 81.9) * mm});
            skPoint(sketch, "E253.MirrorP", {"position": v(-834.12, 129.9) * mm});
            skPoint(sketch, "E254.MirrorP", {"position": v(-832.12, 359.4) * mm});
            skLineSegment(sketch, "E255.MirrorCS", {"start": v(-840.37, 360.9) * mm, "end": v(-840.37, 445.9) * mm});
            skPoint(sketch, "E256.MirrorP", {"position": v(-840.37, 170.9) * mm});
            skPoint(sketch, "E257.MirrorP", {"position": v(-834.12, 315.9) * mm});
            skPoint(sketch, "E258.MirrorP", {"position": v(-832.12, 80.4) * mm});
            skPoint(sketch, "E259.MirrorP", {"position": v(-836.12, 359.4) * mm});
            skPoint(sketch, "E260.MirrorP", {"position": v(-827.87, 363.9) * mm});
            skPoint(sketch, "E261.MirrorP", {"position": v(-834.12, 360.9) * mm});
            skPoint(sketch, "E262.MirrorP", {"position": v(-827.87, 270.9) * mm});
            skPoint(sketch, "E263.MirrorP", {"position": v(-834.12, 408.9) * mm});
            skLineSegment(sketch, "E264.MirrorCS", {"start": v(-840.37, 81.9) * mm, "end": v(-840.37, 166.9) * mm});
            skPoint(sketch, "E265.MirrorP", {"position": v(-827.87, 456.9) * mm});
            skSolve(sketch);
        }
        {
            var Q0;
            Q0=makeQuery(id+"F5.imprint","IMPRINT",FACE,{"disambiguationData":[TD([[makeQuery(id+"F5.imprint","IMPRINT",EDGE,{"derivedFrom":sQuery(id+"F5.wireOp",EDGE,"E179.MirrorCS")}),1.0]])]});
            var Q1;
            Q1=makeQuery(id+"F5.imprint","IMPRINT",FACE,{"disambiguationData":[TD([[makeQuery(id+"F5.imprint","IMPRINT",EDGE,{"derivedFrom":sQuery(id+"F5.wireOp",EDGE,"E65.MirrorCS")}),-1.0]])]});
            extrude(context, id + "F6", {"entities" : qUnion([Q0, Q1]), "depth" : (500 - 18.25 * 2) * mm});
        }
        {
            var Q0;
            Q0=makeQuery(id+"F4.opExtrude","SWEPT_FACE",FACE,{"disambiguationData":[OSD([sQuery(id+"F2.wireOp",EDGE,"E25.MirrorCS")])]});
            var sketch = newSketch(context, id + "F7", { "sketchPlane" : qUnion([Q0])});
            skLineSegment(sketch, "E266.MirrorCS", {"start": v(-453.34, 104.97) * mm, "end": v(-453.59, 104.97) * mm});
            skLineSegment(sketch, "E267.MirrorCS", {"start": v(-449.34, 15.97) * mm, "end": v(-449.34, 18.97) * mm});
            skLineSegment(sketch, "E268.MirrorCS", {"start": v(-449.34, 15.97) * mm, "end": v(-445.09, 15.97) * mm});
            skLineSegment(sketch, "E269.MirrorCS", {"start": v(-449.34, 111.97) * mm, "end": v(-449.34, 108.97) * mm});
            skLineSegment(sketch, "E270.MirrorCS", {"start": v(-449.34, 18.97) * mm, "end": v(-453.34, 18.97) * mm});
            skLineSegment(sketch, "E271.MirrorCS", {"start": v(-453.34, 15.97) * mm, "end": v(-453.34, 18.97) * mm});
            skLineSegment(sketch, "E272.MirrorCS", {"start": v(-451.34, 111.97) * mm, "end": v(-453.34, 111.97) * mm});
            skLineSegment(sketch, "E273.MirrorCS", {"start": v(-453.34, 111.97) * mm, "end": v(-453.34, 104.97) * mm});
            skArc(sketch, "E274.MirrorCS", {"start": v(-445.09, 36.47) * mm, "mid": v(-447.59, 38.97) * mm, "end": v(-445.09, 41.47) * mm});
            skLineSegment(sketch, "E275.MirrorCS", {"start": v(-457.59, 15.97) * mm, "end": v(-453.34, 15.97) * mm});
            skLineSegment(sketch, "E276.MirrorCS", {"start": v(-453.34, 111.97) * mm, "end": v(-449.34, 111.97) * mm});
            skArc(sketch, "E277.MirrorCS", {"start": v(-445.09, 86.47) * mm, "mid": v(-447.59, 88.97) * mm, "end": v(-445.09, 91.47) * mm});
            skArc(sketch, "E278.MirrorCS", {"start": v(-457.59, 100.97) * mm, "mid": v(-456.42, 103.8) * mm, "end": v(-453.59, 104.97) * mm});
            skLineSegment(sketch, "E279.MirrorCS", {"start": v(-445.09, 63.97) * mm, "end": v(-445.09, 41.47) * mm});
            skPoint(sketch, "E280.MirrorP", {"position": v(-457.59, 104.97) * mm});
            skLineSegment(sketch, "E281.MirrorCS", {"start": v(-445.09, 63.97) * mm, "end": v(-445.09, 86.47) * mm});
            skPoint(sketch, "E282.MirrorP", {"position": v(-451.34, 63.97) * mm});
            skLineSegment(sketch, "E283.MirrorCS", {"start": v(-445.09, 15.97) * mm, "end": v(-445.09, 36.47) * mm});
            skLineSegment(sketch, "E284.MirrorCS", {"start": v(-445.09, 91.47) * mm, "end": v(-445.09, 108.97) * mm});
            skLineSegment(sketch, "E285.MirrorCS", {"start": v(-445.09, 41.47) * mm, "end": v(-445.09, 88.97) * mm});
            skLineSegment(sketch, "E286.MirrorCS", {"start": v(-457.59, 15.97) * mm, "end": v(-457.59, 100.97) * mm});
            skLineSegment(sketch, "E287", {"start": v(-500.06, 131.66) * mm, "end": v(-500.06, -10.3) * mm});
            skLineSegment(sketch, "E288.MirrorCS", {"start": v(-546.79, 104.97) * mm, "end": v(-546.54, 104.97) * mm});
            skArc(sketch, "E289.MirrorCS", {"start": v(-542.54, 100.97) * mm, "mid": v(-543.7, 103.8) * mm, "end": v(-546.54, 104.97) * mm});
            skLineSegment(sketch, "E290.MirrorCS", {"start": v(-550.79, 15.97) * mm, "end": v(-550.79, 18.97) * mm});
            skLineSegment(sketch, "E291.MirrorCS", {"start": v(-550.79, 111.97) * mm, "end": v(-550.79, 108.97) * mm});
            skLineSegment(sketch, "E292.MirrorCS", {"start": v(-548.79, 111.97) * mm, "end": v(-546.79, 111.97) * mm});
            skLineSegment(sketch, "E293.MirrorCS", {"start": v(-550.79, 15.97) * mm, "end": v(-555.04, 15.97) * mm});
            skLineSegment(sketch, "E294.MirrorCS", {"start": v(-550.79, 18.97) * mm, "end": v(-546.79, 18.97) * mm});
            skLineSegment(sketch, "E295.MirrorCS", {"start": v(-546.79, 15.97) * mm, "end": v(-546.79, 18.97) * mm});
            skLineSegment(sketch, "E296.MirrorCS", {"start": v(-546.79, 111.97) * mm, "end": v(-546.79, 104.97) * mm});
            skArc(sketch, "E297.MirrorCS", {"start": v(-555.04, 36.47) * mm, "mid": v(-552.54, 38.97) * mm, "end": v(-555.04, 41.47) * mm});
            skLineSegment(sketch, "E298.MirrorCS", {"start": v(-546.79, 111.97) * mm, "end": v(-550.79, 111.97) * mm});
            skLineSegment(sketch, "E299.MirrorCS", {"start": v(-548.79, 111.97) * mm, "end": v(-550.79, 111.97) * mm});
            skLineSegment(sketch, "E300.MirrorCS", {"start": v(-542.54, 15.97) * mm, "end": v(-546.79, 15.97) * mm});
            skArc(sketch, "E301.MirrorCS", {"start": v(-555.04, 86.47) * mm, "mid": v(-552.54, 88.97) * mm, "end": v(-555.04, 91.47) * mm});
            skLineSegment(sketch, "E302.MirrorCS", {"start": v(-555.04, 91.47) * mm, "end": v(-555.04, 108.97) * mm});
            skLineSegment(sketch, "E303.MirrorCS", {"start": v(-555.04, 41.47) * mm, "end": v(-555.04, 88.97) * mm});
            skPoint(sketch, "E304.MirrorP", {"position": v(-546.79, 14.47) * mm});
            skPoint(sketch, "E305.MirrorP", {"position": v(-555.04, 111.97) * mm});
            skLineSegment(sketch, "E306.MirrorCS", {"start": v(-555.04, 15.97) * mm, "end": v(-555.04, 36.47) * mm});
            skPoint(sketch, "E307.MirrorP", {"position": v(-542.54, 104.97) * mm});
            skPoint(sketch, "E308.MirrorP", {"position": v(-550.17, 66.4) * mm});
            skPoint(sketch, "E309.MirrorP", {"position": v(-548.79, 63.97) * mm});
            skLineSegment(sketch, "E310.MirrorCS", {"start": v(-555.04, 63.97) * mm, "end": v(-555.04, 86.47) * mm});
            skPoint(sketch, "E311.MirrorP", {"position": v(-548.79, 15.97) * mm});
            skPoint(sketch, "E312.MirrorP", {"position": v(-550.79, 14.47) * mm});
            skLineSegment(sketch, "E313.MirrorCS", {"start": v(-555.04, 63.97) * mm, "end": v(-555.04, 41.47) * mm});
            skLineSegment(sketch, "E314.MirrorCS", {"start": v(-542.54, 15.97) * mm, "end": v(-542.54, 100.97) * mm});
            skLineSegment(sketch, "E315", {"start": v(-451.34, 63.97) * mm, "end": v(-451.34, 156.97) * mm});
            skLineSegment(sketch, "E316", {"start": v(-449.34, 108.97) * mm, "end": v(-457.59, 108.97) * mm, "construction": true});
            skLineSegment(sketch, "E317.MirrorCS", {"start": v(-451.34, 204.97) * mm, "end": v(-449.34, 204.97) * mm});
            skLineSegment(sketch, "E318.MirrorCS", {"start": v(-453.34, 197.97) * mm, "end": v(-453.59, 197.97) * mm});
            skLineSegment(sketch, "E319.MirrorCS", {"start": v(-449.34, 108.97) * mm, "end": v(-449.34, 111.97) * mm});
            skLineSegment(sketch, "E320.MirrorCS", {"start": v(-449.34, 204.97) * mm, "end": v(-449.34, 201.97) * mm});
            skLineSegment(sketch, "E321.MirrorCS", {"start": v(-453.34, 108.97) * mm, "end": v(-453.34, 111.97) * mm});
            skLineSegment(sketch, "E322.MirrorCS", {"start": v(-451.34, 204.97) * mm, "end": v(-453.34, 204.97) * mm});
            skLineSegment(sketch, "E323.MirrorCS", {"start": v(-453.34, 204.97) * mm, "end": v(-453.34, 197.97) * mm});
            skArc(sketch, "E324.MirrorCS", {"start": v(-445.09, 129.47) * mm, "mid": v(-447.59, 131.97) * mm, "end": v(-445.09, 134.47) * mm});
            skLineSegment(sketch, "E325.MirrorCS", {"start": v(-457.59, 108.97) * mm, "end": v(-453.34, 108.97) * mm});
            skLineSegment(sketch, "E326.MirrorCS", {"start": v(-453.34, 204.97) * mm, "end": v(-449.34, 204.97) * mm});
            skArc(sketch, "E327.MirrorCS", {"start": v(-445.09, 179.47) * mm, "mid": v(-447.59, 181.97) * mm, "end": v(-445.09, 184.47) * mm});
            skArc(sketch, "E328.MirrorCS", {"start": v(-457.59, 193.97) * mm, "mid": v(-456.42, 196.8) * mm, "end": v(-453.59, 197.97) * mm});
            skLineSegment(sketch, "E329.MirrorCS", {"start": v(-445.09, 156.97) * mm, "end": v(-445.09, 134.47) * mm});
            skPoint(sketch, "E330.MirrorP", {"position": v(-457.59, 197.97) * mm});
            skLineSegment(sketch, "E331.MirrorCS", {"start": v(-445.09, 156.97) * mm, "end": v(-445.09, 179.47) * mm});
            skPoint(sketch, "E332.MirrorP", {"position": v(-451.34, 156.97) * mm});
            skLineSegment(sketch, "E333.MirrorCS", {"start": v(-445.09, 108.97) * mm, "end": v(-445.09, 129.47) * mm});
            skLineSegment(sketch, "E334.MirrorCS", {"start": v(-445.09, 184.47) * mm, "end": v(-445.09, 201.97) * mm});
            skLineSegment(sketch, "E335.MirrorCS", {"start": v(-445.09, 134.47) * mm, "end": v(-445.09, 181.97) * mm});
            skLineSegment(sketch, "E336.MirrorCS", {"start": v(-457.59, 108.97) * mm, "end": v(-457.59, 193.97) * mm});
            skLineSegment(sketch, "E337", {"start": v(-449.34, 201.97) * mm, "end": v(-457.59, 201.97) * mm, "construction": true});
            skLineSegment(sketch, "E338.MirrorCS", {"start": v(-451.34, 297.97) * mm, "end": v(-449.34, 297.97) * mm});
            skLineSegment(sketch, "E339.MirrorCS", {"start": v(-453.34, 290.97) * mm, "end": v(-453.59, 290.97) * mm});
            skLineSegment(sketch, "E340.MirrorCS", {"start": v(-449.34, 201.97) * mm, "end": v(-449.34, 204.97) * mm});
            skLineSegment(sketch, "E341.MirrorCS", {"start": v(-449.34, 297.97) * mm, "end": v(-449.34, 294.97) * mm});
            skLineSegment(sketch, "E342.MirrorCS", {"start": v(-449.34, 204.97) * mm, "end": v(-453.34, 204.97) * mm});
            skLineSegment(sketch, "E343.MirrorCS", {"start": v(-453.34, 201.97) * mm, "end": v(-453.34, 204.97) * mm});
            skLineSegment(sketch, "E344.MirrorCS", {"start": v(-451.34, 297.97) * mm, "end": v(-453.34, 297.97) * mm});
            skLineSegment(sketch, "E345.MirrorCS", {"start": v(-453.34, 297.97) * mm, "end": v(-453.34, 290.97) * mm});
            skArc(sketch, "E346.MirrorCS", {"start": v(-445.09, 222.47) * mm, "mid": v(-447.59, 224.97) * mm, "end": v(-445.09, 227.47) * mm});
            skLineSegment(sketch, "E347.MirrorCS", {"start": v(-457.59, 201.97) * mm, "end": v(-453.34, 201.97) * mm});
            skLineSegment(sketch, "E348.MirrorCS", {"start": v(-453.34, 297.97) * mm, "end": v(-449.34, 297.97) * mm});
            skArc(sketch, "E349.MirrorCS", {"start": v(-445.09, 272.47) * mm, "mid": v(-447.59, 274.97) * mm, "end": v(-445.09, 277.47) * mm});
            skArc(sketch, "E350.MirrorCS", {"start": v(-457.59, 286.97) * mm, "mid": v(-456.42, 289.8) * mm, "end": v(-453.59, 290.97) * mm});
            skLineSegment(sketch, "E351.MirrorCS", {"start": v(-445.09, 249.97) * mm, "end": v(-445.09, 227.47) * mm});
            skPoint(sketch, "E352.MirrorP", {"position": v(-457.59, 290.97) * mm});
            skLineSegment(sketch, "E353.MirrorCS", {"start": v(-445.09, 249.97) * mm, "end": v(-445.09, 272.47) * mm});
            skPoint(sketch, "E354.MirrorP", {"position": v(-451.34, 249.97) * mm});
            skLineSegment(sketch, "E355.MirrorCS", {"start": v(-445.09, 201.97) * mm, "end": v(-445.09, 222.47) * mm});
            skLineSegment(sketch, "E356.MirrorCS", {"start": v(-445.09, 277.47) * mm, "end": v(-445.09, 294.97) * mm});
            skLineSegment(sketch, "E357.MirrorCS", {"start": v(-445.09, 227.47) * mm, "end": v(-445.09, 274.97) * mm});
            skLineSegment(sketch, "E358.MirrorCS", {"start": v(-457.59, 201.97) * mm, "end": v(-457.59, 286.97) * mm});
            skLineSegment(sketch, "E359", {"start": v(-449.34, 294.97) * mm, "end": v(-457.59, 294.97) * mm, "construction": true});
            skLineSegment(sketch, "E360.MirrorCS", {"start": v(-451.34, 390.97) * mm, "end": v(-449.34, 390.97) * mm});
            skLineSegment(sketch, "E361.MirrorCS", {"start": v(-453.34, 383.97) * mm, "end": v(-453.59, 383.97) * mm});
            skLineSegment(sketch, "E362.MirrorCS", {"start": v(-449.34, 294.97) * mm, "end": v(-449.34, 297.97) * mm});
            skLineSegment(sketch, "E363.MirrorCS", {"start": v(-449.34, 390.97) * mm, "end": v(-449.34, 387.97) * mm});
            skLineSegment(sketch, "E364.MirrorCS", {"start": v(-449.34, 297.97) * mm, "end": v(-453.34, 297.97) * mm});
            skLineSegment(sketch, "E365.MirrorCS", {"start": v(-449.34, 387.97) * mm, "end": v(-445.09, 387.97) * mm});
            skLineSegment(sketch, "E366.MirrorCS", {"start": v(-453.34, 294.97) * mm, "end": v(-453.34, 297.97) * mm});
            skLineSegment(sketch, "E367.MirrorCS", {"start": v(-451.34, 390.97) * mm, "end": v(-453.34, 390.97) * mm});
            skLineSegment(sketch, "E368.MirrorCS", {"start": v(-453.34, 390.97) * mm, "end": v(-453.34, 383.97) * mm});
            skArc(sketch, "E369.MirrorCS", {"start": v(-445.09, 315.47) * mm, "mid": v(-447.59, 317.97) * mm, "end": v(-445.09, 320.47) * mm});
            skLineSegment(sketch, "E370.MirrorCS", {"start": v(-457.59, 294.97) * mm, "end": v(-453.34, 294.97) * mm});
            skLineSegment(sketch, "E371.MirrorCS", {"start": v(-453.34, 390.97) * mm, "end": v(-449.34, 390.97) * mm});
            skArc(sketch, "E372.MirrorCS", {"start": v(-445.09, 365.47) * mm, "mid": v(-447.59, 367.97) * mm, "end": v(-445.09, 370.47) * mm});
            skArc(sketch, "E373.MirrorCS", {"start": v(-457.59, 379.97) * mm, "mid": v(-456.42, 382.8) * mm, "end": v(-453.59, 383.97) * mm});
            skLineSegment(sketch, "E374.MirrorCS", {"start": v(-445.09, 342.97) * mm, "end": v(-445.09, 320.47) * mm});
            skPoint(sketch, "E375.MirrorP", {"position": v(-457.59, 383.97) * mm});
            skLineSegment(sketch, "E376.MirrorCS", {"start": v(-445.09, 342.97) * mm, "end": v(-445.09, 365.47) * mm});
            skPoint(sketch, "E377.MirrorP", {"position": v(-451.34, 342.97) * mm});
            skLineSegment(sketch, "E378.MirrorCS", {"start": v(-445.09, 294.97) * mm, "end": v(-445.09, 315.47) * mm});
            skLineSegment(sketch, "E379.MirrorCS", {"start": v(-445.09, 370.47) * mm, "end": v(-445.09, 387.97) * mm});
            skLineSegment(sketch, "E380.MirrorCS", {"start": v(-445.09, 320.47) * mm, "end": v(-445.09, 367.97) * mm});
            skLineSegment(sketch, "E381.MirrorCS", {"start": v(-457.59, 294.97) * mm, "end": v(-457.59, 379.97) * mm});
            skLineSegment(sketch, "E382", {"start": v(-449.34, 387.97) * mm, "end": v(-457.59, 387.97) * mm, "construction": true});
            skLineSegment(sketch, "E383.MirrorCS", {"start": v(-546.79, 197.97) * mm, "end": v(-546.54, 197.97) * mm});
            skArc(sketch, "E384.MirrorCS", {"start": v(-542.54, 193.97) * mm, "mid": v(-543.7, 196.8) * mm, "end": v(-546.54, 197.97) * mm});
            skLineSegment(sketch, "E385.MirrorCS", {"start": v(-550.79, 108.97) * mm, "end": v(-550.79, 111.97) * mm});
            skLineSegment(sketch, "E386.MirrorCS", {"start": v(-550.79, 204.97) * mm, "end": v(-550.79, 201.97) * mm});
            skLineSegment(sketch, "E387.MirrorCS", {"start": v(-548.79, 204.97) * mm, "end": v(-546.79, 204.97) * mm});
            skLineSegment(sketch, "E388.MirrorCS", {"start": v(-550.79, 111.97) * mm, "end": v(-546.79, 111.97) * mm});
            skLineSegment(sketch, "E389.MirrorCS", {"start": v(-546.79, 108.97) * mm, "end": v(-546.79, 111.97) * mm});
            skLineSegment(sketch, "E390.MirrorCS", {"start": v(-546.79, 204.97) * mm, "end": v(-546.79, 197.97) * mm});
            skArc(sketch, "E391.MirrorCS", {"start": v(-555.04, 129.47) * mm, "mid": v(-552.54, 131.97) * mm, "end": v(-555.04, 134.47) * mm});
            skLineSegment(sketch, "E392.MirrorCS", {"start": v(-546.79, 204.97) * mm, "end": v(-550.79, 204.97) * mm});
            skLineSegment(sketch, "E393.MirrorCS", {"start": v(-548.79, 204.97) * mm, "end": v(-550.79, 204.97) * mm});
            skLineSegment(sketch, "E394.MirrorCS", {"start": v(-542.54, 108.97) * mm, "end": v(-546.79, 108.97) * mm});
            skArc(sketch, "E395.MirrorCS", {"start": v(-555.04, 179.47) * mm, "mid": v(-552.54, 181.97) * mm, "end": v(-555.04, 184.47) * mm});
            skLineSegment(sketch, "E396.MirrorCS", {"start": v(-555.04, 184.47) * mm, "end": v(-555.04, 201.97) * mm});
            skLineSegment(sketch, "E397.MirrorCS", {"start": v(-555.04, 134.47) * mm, "end": v(-555.04, 181.97) * mm});
            skPoint(sketch, "E398.MirrorP", {"position": v(-546.79, 107.47) * mm});
            skPoint(sketch, "E399.MirrorP", {"position": v(-555.04, 204.97) * mm});
            skLineSegment(sketch, "E400.MirrorCS", {"start": v(-555.04, 108.97) * mm, "end": v(-555.04, 129.47) * mm});
            skPoint(sketch, "E401.MirrorP", {"position": v(-542.54, 197.97) * mm});
            skPoint(sketch, "E402.MirrorP", {"position": v(-550.17, 159.4) * mm});
            skPoint(sketch, "E403.MirrorP", {"position": v(-548.79, 156.97) * mm});
            skLineSegment(sketch, "E404.MirrorCS", {"start": v(-555.04, 156.97) * mm, "end": v(-555.04, 179.47) * mm});
            skPoint(sketch, "E405.MirrorP", {"position": v(-548.79, 108.97) * mm});
            skPoint(sketch, "E406.MirrorP", {"position": v(-550.79, 107.47) * mm});
            skLineSegment(sketch, "E407.MirrorCS", {"start": v(-555.04, 156.97) * mm, "end": v(-555.04, 134.47) * mm});
            skLineSegment(sketch, "E408.MirrorCS", {"start": v(-542.54, 108.97) * mm, "end": v(-542.54, 193.97) * mm});
            skLineSegment(sketch, "E409.MirrorCS", {"start": v(-546.79, 290.97) * mm, "end": v(-546.54, 290.97) * mm});
            skArc(sketch, "E410.MirrorCS", {"start": v(-542.54, 286.97) * mm, "mid": v(-543.7, 289.8) * mm, "end": v(-546.54, 290.97) * mm});
            skLineSegment(sketch, "E411.MirrorCS", {"start": v(-550.79, 201.97) * mm, "end": v(-550.79, 204.97) * mm});
            skLineSegment(sketch, "E412.MirrorCS", {"start": v(-550.79, 297.97) * mm, "end": v(-550.79, 294.97) * mm});
            skLineSegment(sketch, "E413.MirrorCS", {"start": v(-548.79, 297.97) * mm, "end": v(-546.79, 297.97) * mm});
            skLineSegment(sketch, "E414.MirrorCS", {"start": v(-550.79, 204.97) * mm, "end": v(-546.79, 204.97) * mm});
            skLineSegment(sketch, "E415.MirrorCS", {"start": v(-546.79, 201.97) * mm, "end": v(-546.79, 204.97) * mm});
            skLineSegment(sketch, "E416.MirrorCS", {"start": v(-546.79, 297.97) * mm, "end": v(-546.79, 290.97) * mm});
            skArc(sketch, "E417.MirrorCS", {"start": v(-555.04, 222.47) * mm, "mid": v(-552.54, 224.97) * mm, "end": v(-555.04, 227.47) * mm});
            skLineSegment(sketch, "E418.MirrorCS", {"start": v(-546.79, 297.97) * mm, "end": v(-550.79, 297.97) * mm});
            skLineSegment(sketch, "E419.MirrorCS", {"start": v(-548.79, 297.97) * mm, "end": v(-550.79, 297.97) * mm});
            skLineSegment(sketch, "E420.MirrorCS", {"start": v(-542.54, 201.97) * mm, "end": v(-546.79, 201.97) * mm});
            skArc(sketch, "E421.MirrorCS", {"start": v(-555.04, 272.47) * mm, "mid": v(-552.54, 274.97) * mm, "end": v(-555.04, 277.47) * mm});
            skLineSegment(sketch, "E422.MirrorCS", {"start": v(-555.04, 277.47) * mm, "end": v(-555.04, 294.97) * mm});
            skLineSegment(sketch, "E423.MirrorCS", {"start": v(-555.04, 227.47) * mm, "end": v(-555.04, 274.97) * mm});
            skPoint(sketch, "E424.MirrorP", {"position": v(-546.79, 200.47) * mm});
            skPoint(sketch, "E425.MirrorP", {"position": v(-555.04, 297.97) * mm});
            skLineSegment(sketch, "E426.MirrorCS", {"start": v(-555.04, 201.97) * mm, "end": v(-555.04, 222.47) * mm});
            skPoint(sketch, "E427.MirrorP", {"position": v(-542.54, 290.97) * mm});
            skPoint(sketch, "E428.MirrorP", {"position": v(-550.17, 252.4) * mm});
            skPoint(sketch, "E429.MirrorP", {"position": v(-548.79, 249.97) * mm});
            skLineSegment(sketch, "E430.MirrorCS", {"start": v(-555.04, 249.97) * mm, "end": v(-555.04, 272.47) * mm});
            skPoint(sketch, "E431.MirrorP", {"position": v(-548.79, 201.97) * mm});
            skPoint(sketch, "E432.MirrorP", {"position": v(-550.79, 200.47) * mm});
            skLineSegment(sketch, "E433.MirrorCS", {"start": v(-555.04, 249.97) * mm, "end": v(-555.04, 227.47) * mm});
            skLineSegment(sketch, "E434.MirrorCS", {"start": v(-542.54, 201.97) * mm, "end": v(-542.54, 286.97) * mm});
            skLineSegment(sketch, "E435.MirrorCS", {"start": v(-546.79, 383.97) * mm, "end": v(-546.54, 383.97) * mm});
            skArc(sketch, "E436.MirrorCS", {"start": v(-542.54, 379.97) * mm, "mid": v(-543.7, 382.8) * mm, "end": v(-546.54, 383.97) * mm});
            skLineSegment(sketch, "E437.MirrorCS", {"start": v(-550.79, 294.97) * mm, "end": v(-550.79, 297.97) * mm});
            skLineSegment(sketch, "E438.MirrorCS", {"start": v(-550.79, 390.97) * mm, "end": v(-550.79, 387.97) * mm});
            skLineSegment(sketch, "E439.MirrorCS", {"start": v(-548.79, 390.97) * mm, "end": v(-546.79, 390.97) * mm});
            skLineSegment(sketch, "E440.MirrorCS", {"start": v(-550.79, 297.97) * mm, "end": v(-546.79, 297.97) * mm});
            skLineSegment(sketch, "E441.MirrorCS", {"start": v(-550.79, 387.97) * mm, "end": v(-555.04, 387.97) * mm});
            skLineSegment(sketch, "E442.MirrorCS", {"start": v(-546.79, 294.97) * mm, "end": v(-546.79, 297.97) * mm});
            skLineSegment(sketch, "E443.MirrorCS", {"start": v(-546.79, 390.97) * mm, "end": v(-546.79, 383.97) * mm});
            skArc(sketch, "E444.MirrorCS", {"start": v(-555.04, 315.47) * mm, "mid": v(-552.54, 317.97) * mm, "end": v(-555.04, 320.47) * mm});
            skLineSegment(sketch, "E445.MirrorCS", {"start": v(-546.79, 390.97) * mm, "end": v(-550.79, 390.97) * mm});
            skLineSegment(sketch, "E446.MirrorCS", {"start": v(-548.79, 390.97) * mm, "end": v(-550.79, 390.97) * mm});
            skLineSegment(sketch, "E447.MirrorCS", {"start": v(-542.54, 294.97) * mm, "end": v(-546.79, 294.97) * mm});
            skArc(sketch, "E448.MirrorCS", {"start": v(-555.04, 365.47) * mm, "mid": v(-552.54, 367.97) * mm, "end": v(-555.04, 370.47) * mm});
            skLineSegment(sketch, "E449.MirrorCS", {"start": v(-555.04, 370.47) * mm, "end": v(-555.04, 387.97) * mm});
            skLineSegment(sketch, "E450.MirrorCS", {"start": v(-555.04, 320.47) * mm, "end": v(-555.04, 367.97) * mm});
            skPoint(sketch, "E451.MirrorP", {"position": v(-546.79, 293.47) * mm});
            skPoint(sketch, "E452.MirrorP", {"position": v(-555.04, 390.97) * mm});
            skLineSegment(sketch, "E453.MirrorCS", {"start": v(-555.04, 294.97) * mm, "end": v(-555.04, 315.47) * mm});
            skPoint(sketch, "E454.MirrorP", {"position": v(-542.54, 383.97) * mm});
            skPoint(sketch, "E455.MirrorP", {"position": v(-550.17, 345.4) * mm});
            skPoint(sketch, "E456.MirrorP", {"position": v(-548.79, 342.97) * mm});
            skLineSegment(sketch, "E457.MirrorCS", {"start": v(-555.04, 342.97) * mm, "end": v(-555.04, 365.47) * mm});
            skPoint(sketch, "E458.MirrorP", {"position": v(-548.79, 294.97) * mm});
            skPoint(sketch, "E459.MirrorP", {"position": v(-550.79, 293.47) * mm});
            skLineSegment(sketch, "E460.MirrorCS", {"start": v(-555.04, 342.97) * mm, "end": v(-555.04, 320.47) * mm});
            skLineSegment(sketch, "E461.MirrorCS", {"start": v(-542.54, 294.97) * mm, "end": v(-542.54, 379.97) * mm});
            skSolve(sketch);
        }
        {
            var Q0;
            Q0=makeQuery(id+"F7.imprint","IMPRINT",FACE,{"disambiguationData":[TD([[makeQuery(id+"F7.imprint","IMPRINT",EDGE,{"derivedFrom":sQuery(id+"F7.wireOp",EDGE,"E288.MirrorCS")}),-1.0]])]});
            var Q1;
            Q1=makeQuery(id+"F7.imprint","IMPRINT",FACE,{"disambiguationData":[TD([[makeQuery(id+"F7.imprint","IMPRINT",EDGE,{"derivedFrom":sQuery(id+"F7.wireOp",EDGE,"E266.MirrorCS")}),1.0]])]});
            extrude(context, id + "F8", {"entities" : qUnion([Q0, Q1]), "depth" : 663.5 * mm});
        }
        {
            var Q0;
            Q0=makeQuery(id+"F8.opExtrude","SWEPT_FACE",FACE,{"disambiguationData":[OSD([sQuery(id+"F7.wireOp",EDGE,"E286.MirrorCS")])]});
            var sketch = newSketch(context, id + "F9", { "sketchPlane" : qUnion([Q0])});
            skLineSegment(sketch, "E462.bottom", {"start": v(-331.75, 15.97) * mm, "end": v(331.75, 15.97) * mm});
            skLineSegment(sketch, "E462.top", {"start": v(-331.75, 390.97) * mm, "end": v(331.75, 390.97) * mm});
            skLineSegment(sketch, "E462.left", {"start": v(-331.75, 15.97) * mm, "end": v(-331.75, 390.97) * mm});
            skLineSegment(sketch, "E462.right", {"start": v(331.75, 15.97) * mm, "end": v(331.75, 390.97) * mm});
            skLineSegment(sketch, "E463", {"start": v(331.75, 15.97) * mm, "end": v(181.75, 15.97) * mm});
            skLineSegment(sketch, "E464.bottom", {"start": v(-91.75, 320.97) * mm, "end": v(-211.75, 320.97) * mm});
            skLineSegment(sketch, "E464.top", {"start": v(-91.75, 160.97) * mm, "end": v(-211.75, 160.97) * mm});
            skLineSegment(sketch, "E464.left", {"start": v(-81.75, 310.97) * mm, "end": v(-81.75, 170.97) * mm});
            skLineSegment(sketch, "E464.right", {"start": v(-221.75, 310.97) * mm, "end": v(-221.75, 170.97) * mm});
            skPoint(sketch, "E464.middle", {"position": v(-151.75, 240.97) * mm});
            skPoint(sketch, "E465.visualSharp", {"position": v(-221.75, 320.97) * mm});
            skArc(sketch, "E465.filletArc", {"start": v(-211.75, 320.97) * mm, "mid": v(-218.82, 318.04) * mm, "end": v(-221.75, 310.97) * mm});
            skPoint(sketch, "E466.visualSharp", {"position": v(-81.75, 320.97) * mm});
            skArc(sketch, "E466.filletArc", {"start": v(-81.75, 310.97) * mm, "mid": v(-84.68, 318.04) * mm, "end": v(-91.75, 320.97) * mm});
            skPoint(sketch, "E467.visualSharp", {"position": v(-221.75, 160.97) * mm});
            skArc(sketch, "E467.filletArc", {"start": v(-221.75, 170.97) * mm, "mid": v(-218.82, 163.9) * mm, "end": v(-211.75, 160.97) * mm});
            skPoint(sketch, "E468.visualSharp", {"position": v(-81.75, 160.97) * mm});
            skArc(sketch, "E468.filletArc", {"start": v(-91.75, 160.97) * mm, "mid": v(-84.68, 163.9) * mm, "end": v(-81.75, 170.97) * mm});
            skLineSegment(sketch, "E469.bottom", {"start": v(181.75, 15.97) * mm, "end": v(-18.25, 15.97) * mm});
            skLineSegment(sketch, "E469.top", {"start": v(81.75, 315.97) * mm, "end": v(81.75, 315.97) * mm});
            skLineSegment(sketch, "E469.left", {"start": v(181.75, 15.97) * mm, "end": v(181.75, 215.97) * mm});
            skLineSegment(sketch, "E469.right", {"start": v(-18.25, 15.97) * mm, "end": v(-18.25, 215.97) * mm});
            skPoint(sketch, "E470.visualSharp", {"position": v(-18.25, 315.97) * mm});
            skArc(sketch, "E470.filletArc", {"start": v(81.75, 315.97) * mm, "mid": v(11.04, 286.68) * mm, "end": v(-18.25, 215.97) * mm});
            skPoint(sketch, "E471.visualSharp", {"position": v(181.75, 315.97) * mm});
            skArc(sketch, "E471.filletArc", {"start": v(181.75, 215.97) * mm, "mid": v(152.46, 286.68) * mm, "end": v(81.75, 315.97) * mm});
            skLineSegment(sketch, "E472.bottom", {"start": v(-1565.88, 420.8) * mm, "end": v(-1565.88, 420.8) * mm});
            skLineSegment(sketch, "E472.top", {"start": v(-1664.88, 122.8) * mm, "end": v(-1466.88, 122.8) * mm});
            skLineSegment(sketch, "E472.left", {"start": v(-1664.88, 321.8) * mm, "end": v(-1664.88, 122.8) * mm});
            skLineSegment(sketch, "E472.right", {"start": v(-1466.88, 321.8) * mm, "end": v(-1466.88, 122.8) * mm});
            skPoint(sketch, "E473.visualSharp", {"position": v(-1664.88, 420.8) * mm});
            skArc(sketch, "E473.filletArc", {"start": v(-1565.88, 420.8) * mm, "mid": v(-1635.89, 391.8) * mm, "end": v(-1664.88, 321.8) * mm});
            skPoint(sketch, "E474.visualSharp", {"position": v(-1466.88, 420.8) * mm});
            skArc(sketch, "E474.filletArc", {"start": v(-1466.88, 321.8) * mm, "mid": v(-1495.88, 391.8) * mm, "end": v(-1565.88, 420.8) * mm});
            skLineSegment(sketch, "E475.0", {"start": v(-1644.88, 142.8) * mm, "end": v(-1486.88, 142.8) * mm});
            skLineSegment(sketch, "E475.1", {"start": v(-1644.88, 321.8) * mm, "end": v(-1644.88, 142.8) * mm});
            skLineSegment(sketch, "E475.2", {"start": v(-1486.88, 321.8) * mm, "end": v(-1486.88, 142.8) * mm});
            skArc(sketch, "E475.3", {"start": v(-1486.88, 321.8) * mm, "mid": v(-1510.38, 378.02) * mm, "end": v(-1566.88, 400.8) * mm});
            skArc(sketch, "E475.4", {"start": v(-1566.88, 400.8) * mm, "mid": v(-1622.1, 377.31) * mm, "end": v(-1644.88, 321.8) * mm});
            skSolve(sketch);
        }
        {
            var Q0;
            Q0=makeQuery(id+"F9.imprint","IMPRINT",FACE,{"disambiguationData":[TD([[makeQuery(id+"F9.imprint","IMPRINT",EDGE,{"derivedFrom":sQuery(id+"F9.wireOp",EDGE,"E464.bottom")}),1.0]])]});
            var Q1;
            {var subQ1=sQuery(id+"F9.wireOp",EDGE,"E470.filletArc");Q1=makeQuery(id+"F9.imprint","IMPRINT",FACE,{"disambiguationData":[TD([[makeQuery(id+"F9.imprint","IMPRINT",EDGE,{"derivedFrom":subQ1}),1.0]])]});}
            var Q2;
            {var subQ0=sQuery(id+"F9.wireOp",EDGE,"E469.bottom");Q2=makeQuery(id+"F9.imprint","IMPRINT",FACE,{"disambiguationData":[TD([[makeQuery(id+"F9.imprint","IMPRINT",EDGE,{"derivedFrom":subQ0}),-1.0]])]});}
            extrude(context, id + "F10", {"entities" : qUnion([Q0, Q1, Q2]), "operationType" : NewBodyOperationType.REMOVE, "oppositeDirection" : true, "depth" : 12.5 * mm});
        }
        {
            var Q0;
            Q0=makeQuery(id+"F9.imprint","IMPRINT",FACE,{"disambiguationData":[TD([[makeQuery(id+"F9.imprint","IMPRINT",EDGE,{"derivedFrom":sQuery(id+"F9.wireOp",EDGE,"E472.top")}),1.0]])]});
            extrude(context, id + "F11", {"entities" : qUnion([Q0]), "oppositeDirection" : true, "depth" : 12 * mm});
        }
    });
